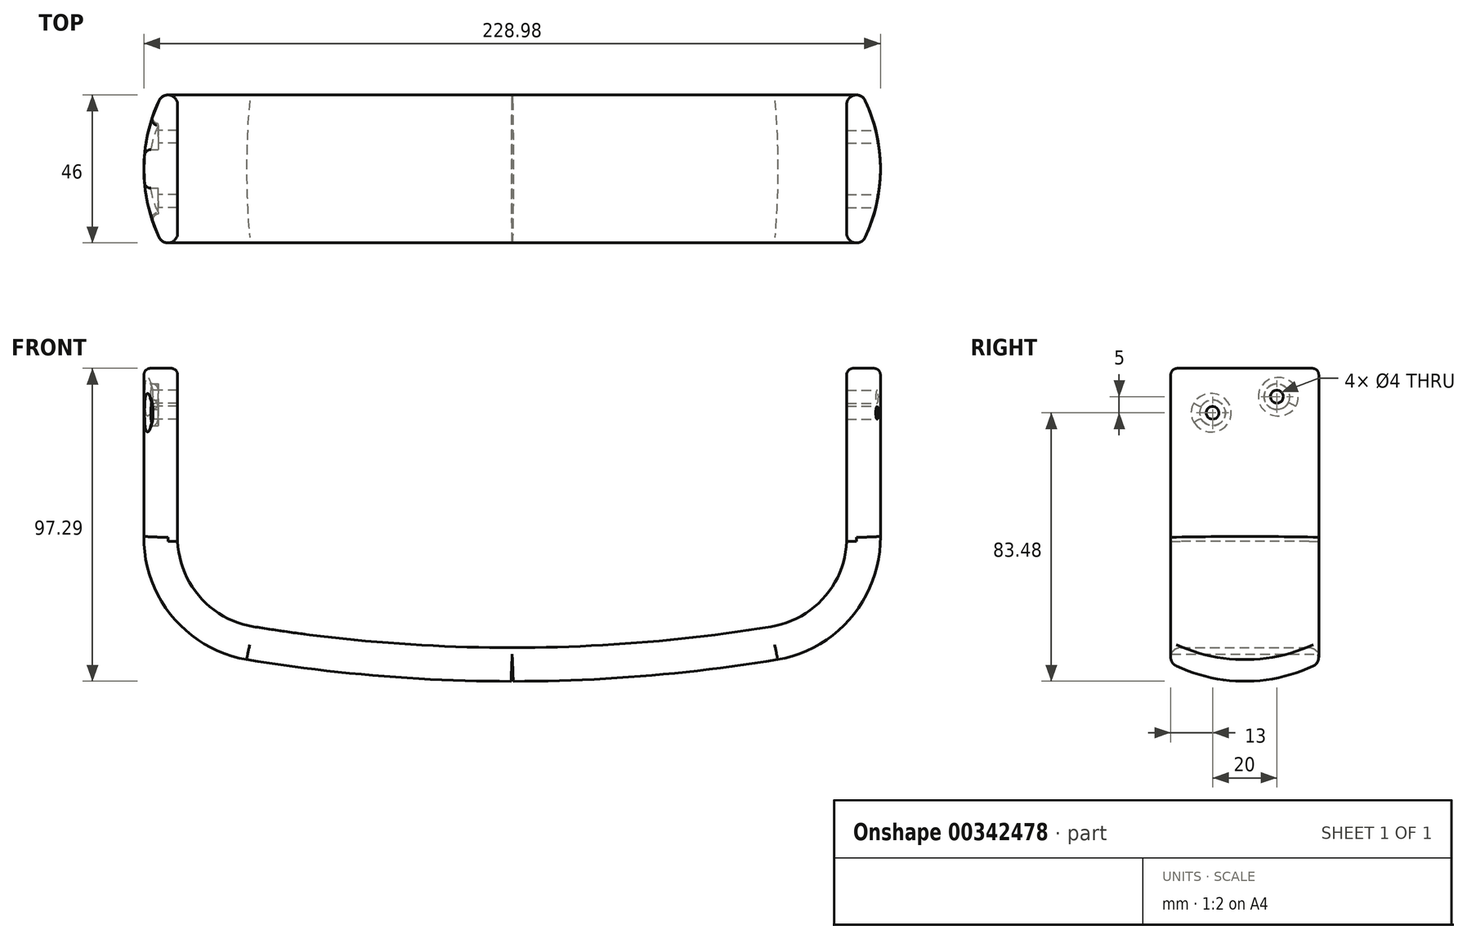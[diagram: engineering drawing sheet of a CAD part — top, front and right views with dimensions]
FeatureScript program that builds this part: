
annotation { "Feature Type Name" : "Feature", "Feature Type Description" : "" }
export const myFeature = defineFeature(function(context is Context, id is Id, definition is map)
    precondition{}
    {
        {
            var Q0;
            Q0=qCreatedBy(makeId("Top.planeOp"),FACE);
            cPlane(context, id + "F0", {"entities" : qUnion([Q0]), "cplaneType" : CPlaneType.OFFSET, "offset" : 55 * mm, "oppositeDirection" : true, "width" : 150 * mm, "height" : 150 * mm});
        }
        {
            var Q0;
            Q0=qCreatedBy(makeId("Front.planeOp"),FACE);
            var sketch = newSketch(context, id + "F1", { "sketchPlane" : qUnion([Q0])});
            skArc(sketch, "E0", {"start": v(0, -90) * mm, "mid": v(-40.56, -88.35) * mm, "end": v(-80.85, -83.42) * mm});
            skLineSegment(sketch, "E1", {"start": v(-106, -53.81) * mm, "end": v(-106, 0) * mm});
            skPoint(sketch, "E2.visualSharp", {"position": v(-106, -78.63) * mm});
            skArc(sketch, "E2.filletArc", {"start": v(-106, -53.81) * mm, "mid": v(-98.86, -73.24) * mm, "end": v(-80.85, -83.42) * mm});
            skArc(sketch, "E3", {"start": v(0, -90) * mm, "mid": v(40.56, -88.35) * mm, "end": v(80.85, -83.42) * mm});
            skLineSegment(sketch, "E4", {"start": v(106, -53.81) * mm, "end": v(106, 0) * mm});
            skPoint(sketch, "E5.visualSharp", {"position": v(106, -78.63) * mm});
            skArc(sketch, "E5.filletArc", {"start": v(80.85, -83.42) * mm, "mid": v(98.86, -73.24) * mm, "end": v(106, -53.81) * mm});
            skSolve(sketch);
        }
        {
            var Q0;
            Q0=qCreatedBy(id+"F0.planeOp",FACE);
            var sketch = newSketch(context, id + "F2", { "sketchPlane" : qUnion([Q0])});
            skCircle(sketch, "E6", {"center": v(-64.47, 0) * mm, "radius": 50 * mm});
            skLineSegment(sketch, "E7", {"start": v(-104, 30.61) * mm, "end": v(-104, -30.61) * mm});
            skCircle(sketch, "E8", {"center": v(-107, 20) * mm, "radius": 3 * mm});
            skCircle(sketch, "E9", {"center": v(-107, -20) * mm, "radius": 3 * mm});
            skSolve(sketch);
        }
        {
            var Q0;
            {var subQ0=sQuery(id+"F2.wireOp",EDGE,"E8");var subQ1=sQuery(id+"F2.wireOp",EDGE,"E6");var subQ2=makeQuery(id+"F2.imprint","INTERSECT",VERTEX,{"derivedFrom":[subQ1,subQ0]});Q0=makeQuery(id+"F2.imprint","IMPRINT",FACE,{"disambiguationData":[TD([[makeQuery(id+"F2.imprint","IMPRINT",EDGE,{"disambiguationData":[TD([[subQ2,-1.0]])],"derivedFrom":subQ1}),1.0]])]});}
            var Q1;
            {var subQ0=sQuery(id+"F2.wireOp",EDGE,"E8");var subQ1=sQuery(id+"F2.wireOp",EDGE,"E7");var subQ2=makeQuery(id+"F2.imprint","INTERSECT",VERTEX,{"disambiguationData":[OD(0.0)],"derivedFrom":[subQ1,subQ0]});Q1=makeQuery(id+"F2.imprint","IMPRINT",FACE,{"disambiguationData":[TD([[makeQuery(id+"F2.imprint","IMPRINT",EDGE,{"disambiguationData":[TD([[subQ2,1.0]])],"derivedFrom":subQ0}),1.0]])]});}
            var Q2;
            {var subQ0=sQuery(id+"F2.wireOp",EDGE,"E9");var subQ1=makeQuery(id+"F2.imprint","INTERSECT",VERTEX,{"derivedFrom":[sQuery(id+"F2.wireOp",EDGE,"E6"),subQ0]});Q2=makeQuery(id+"F2.imprint","IMPRINT",FACE,{"disambiguationData":[TD([[makeQuery(id+"F2.imprint","IMPRINT",EDGE,{"disambiguationData":[TD([[subQ1,1.0]])],"derivedFrom":subQ0}),1.0]])]});}
            var Q3;
            Q3=sQuery(id+"F1.wireOp",EDGE,"E2.filletArc");
            var Q4;
            Q4=sQuery(id+"F1.wireOp",EDGE,"E0");
            sweep(context, id + "F3", {"profiles" : qUnion([Q0, Q1, Q2]), "path" : qUnion([Q3, Q4])});
        }
        {
            var Q0;
            {var subQ0=sQuery(id+"F2.wireOp",EDGE,"E9");var subQ1=makeQuery(id+"F2.imprint","INTERSECT",VERTEX,{"derivedFrom":[sQuery(id+"F2.wireOp",EDGE,"E6"),subQ0]});Q0=makeQuery(id+"F2.imprint","IMPRINT",FACE,{"disambiguationData":[TD([[makeQuery(id+"F2.imprint","IMPRINT",EDGE,{"disambiguationData":[TD([[subQ1,1.0]])],"derivedFrom":subQ0}),1.0]])]});}
            var Q1;
            {var subQ0=sQuery(id+"F2.wireOp",EDGE,"E8");var subQ1=sQuery(id+"F2.wireOp",EDGE,"E6");var subQ2=makeQuery(id+"F2.imprint","INTERSECT",VERTEX,{"derivedFrom":[subQ1,subQ0]});Q1=makeQuery(id+"F2.imprint","IMPRINT",FACE,{"disambiguationData":[TD([[makeQuery(id+"F2.imprint","IMPRINT",EDGE,{"disambiguationData":[TD([[subQ2,-1.0]])],"derivedFrom":subQ1}),1.0]])]});}
            var Q2;
            {var subQ0=sQuery(id+"F2.wireOp",EDGE,"E8");var subQ1=sQuery(id+"F2.wireOp",EDGE,"E7");var subQ2=makeQuery(id+"F2.imprint","INTERSECT",VERTEX,{"disambiguationData":[OD(0.0)],"derivedFrom":[subQ1,subQ0]});Q2=makeQuery(id+"F2.imprint","IMPRINT",FACE,{"disambiguationData":[TD([[makeQuery(id+"F2.imprint","IMPRINT",EDGE,{"disambiguationData":[TD([[subQ2,1.0]])],"derivedFrom":subQ0}),1.0]])]});}
            var Q3;
            Q3=sQuery(id+"F1.wireOp",EDGE,"E1");
            sweep(context, id + "F4", {"operationType" : NewBodyOperationType.ADD, "profiles" : qUnion([Q0, Q1, Q2]), "path" : qUnion([Q3])});
        }
        {
            var Q0;
            Q0=makeQuery(id+"F3.opSweep","SWEPT_BODY",BODY,{"disambiguationData":[OSD([sQuery(id+"F1.wireOp",EDGE,"E0"),sQuery(id+"F2.wireOp",EDGE,"dJ1qTKnS-oq17-yvGb-OPdT-9C4l1Cjw6Oys"),sQuery(id+"F2.wireOp",EDGE,"cmmdOPWz-PyDa-HDoy-eCQN-bhGAXCGdN2CE"),sQuery(id+"F2.wireOp",EDGE,"d8zukWQO-Fq8i-O6NT-Ootf-6UBmwlqmVn10"),sQuery(id+"F2.wireOp",EDGE,"2de68d1f-a85f-48cc-8234-0564c03e4455"),sQuery(id+"F2.wireOp",EDGE,"470c1d83-e3ed-4023-84e1-6bd27dbbabfe"),sQuery(id+"F2.wireOp",EDGE,"wccANr6S-ukYY-3v9n-Jsb8-NzpgIdzZGXg6"),sQuery(id+"F2.wireOp",EDGE,"1fc90554-af48-4865-a39d-4fe91776a1af"),sQuery(id+"F2.wireOp",EDGE,"32e85b6e-5fb4-4d4b-b2f5-fbf4a71d3896")])]});
            var Q1;
            Q1=qCreatedBy(makeId("Right.planeOp"),FACE);
            mirror(context, id + "F5", {"operationType" : NewBodyOperationType.ADD, "entities" : qUnion([Q0]), "mirrorPlane" : qUnion([Q1])});
        }
        {
            var Q0;
            Q0=qCreatedBy(makeId("Right.planeOp"),FACE);
            var sketch = newSketch(context, id + "F6", { "sketchPlane" : qUnion([Q0])});
            skPoint(sketch, "E10", {"position": v(-10, -15) * mm});
            skPoint(sketch, "E11", {"position": v(10, -10) * mm});
            skSolve(sketch);
        }
        {
            var Q0;
            Q0=sQuery(id+"F6.wireOp",VERTEX,"E11");
            var Q1;
            Q1=sQuery(id+"F6.wireOp",VERTEX,"E10");
            var Q2;
            Q2=makeQuery(id+"F3.opSweep","SWEPT_BODY",BODY,{"disambiguationData":[OSD([sQuery(id+"F1.wireOp",EDGE,"E0"),sQuery(id+"F2.wireOp",EDGE,"E6"),sQuery(id+"F2.wireOp",EDGE,"E7"),sQuery(id+"F2.wireOp",EDGE,"E8"),sQuery(id+"F2.wireOp",EDGE,"E9")])]});
            hole(context, id + "F7", {"style" : HoleStyle.SIMPLE, "endStyle" : HoleEndStyle.THROUGH, "holeDiameter" : 4 * mm, "locations" : qUnion([Q0, Q1]), "scope" : qUnion([Q2]), "isTappedThrough" : true});
        }
        {
            var Q0;
            Q0=sQuery(id+"F6.wireOp",VERTEX,"E11");
            var Q1;
            Q1=sQuery(id+"F6.wireOp",VERTEX,"E10");
            var Q2;
            Q2=makeQuery(id+"F3.opSweep","SWEPT_BODY",BODY,{"disambiguationData":[OSD([sQuery(id+"F1.wireOp",EDGE,"E0"),sQuery(id+"F2.wireOp",EDGE,"E6"),sQuery(id+"F2.wireOp",EDGE,"E7"),sQuery(id+"F2.wireOp",EDGE,"E8"),sQuery(id+"F2.wireOp",EDGE,"E9")])]});
            hole(context, id + "F8", {"style" : HoleStyle.SIMPLE, "endStyle" : HoleEndStyle.THROUGH, "oppositeDirection" : true, "holeDiameter" : 4 * mm, "locations" : qUnion([Q0, Q1]), "scope" : qUnion([Q2]), "isTappedThrough" : true});
        }
        {
            var Q0;
            Q0=qCreatedBy(makeId("Right.planeOp"),FACE);
            var sketch = newSketch(context, id + "F9", { "sketchPlane" : qUnion([Q0])});
            skCircle(sketch, "E12", {"center": v(-10, -15) * mm, "radius": 4 * mm});
            skCircle(sketch, "E13", {"center": v(10, -10) * mm, "radius": 4 * mm});
            skSolve(sketch);
        }
        {
            var Q0;
            Q0=qSketchRegion(id+"F9",true);
            extrude(context, id + "F10", {"entities" : qUnion([Q0]), "operationType" : NewBodyOperationType.REMOVE, "oppositeDirection" : true, "depth" : 300 * mm, "hasSecondDirection" : true, "secondDirectionOppositeDirection" : true, "secondDirectionDepth" : 110 * mm});
        }
        {
            var Q0;
            Q0=makeQuery(id+"F4.opSweep","CAP_FACE",FACE,{"disambiguationData":[OSD([sQuery(id+"F1.wireOp",VERTEX,"E1.end"),sQuery(id+"F2.wireOp",EDGE,"dJ1qTKnS-oq17-yvGb-OPdT-9C4l1Cjw6Oys"),sQuery(id+"F2.wireOp",EDGE,"cmmdOPWz-PyDa-HDoy-eCQN-bhGAXCGdN2CE"),sQuery(id+"F2.wireOp",EDGE,"26a42886-8d7c-48d6-a3ba-1dae7db94bb6.filletArc"),sQuery(id+"F2.wireOp",EDGE,"d3881ce3-cca8-404a-a423-4088e6d2d6ec.filletArc")])],"isStart":false});
            var Q1;
            Q1=makeQuery(id+"F5.opPattern","COPY",FACE,{"derivedFrom":makeQuery(id+"F4.opSweep","CAP_FACE",FACE,{"disambiguationData":[OSD([sQuery(id+"F1.wireOp",VERTEX,"E1.end"),sQuery(id+"F2.wireOp",EDGE,"dJ1qTKnS-oq17-yvGb-OPdT-9C4l1Cjw6Oys"),sQuery(id+"F2.wireOp",EDGE,"cmmdOPWz-PyDa-HDoy-eCQN-bhGAXCGdN2CE"),sQuery(id+"F2.wireOp",EDGE,"26a42886-8d7c-48d6-a3ba-1dae7db94bb6.filletArc"),sQuery(id+"F2.wireOp",EDGE,"d3881ce3-cca8-404a-a423-4088e6d2d6ec.filletArc")])],"isStart":false}),"instanceName":"1"});
            var Q2;
            Q2=makeQuery(id+"F10.boolean.opBoolean","INTERSECT",EDGE,{"derivedFrom":[makeQuery(id+"F4.opSweep","SWEPT_FACE",FACE,{"disambiguationData":[OSD([sQuery(id+"F1.wireOp",EDGE,"E1"),sQuery(id+"F2.wireOp",EDGE,"E6")])]}),makeQuery(id+"F10.opExtrude","SWEPT_FACE",FACE,{"disambiguationData":[OSD([sQuery(id+"F9.wireOp",EDGE,"E12")])]})]});
            var Q3;
            Q3=makeQuery(id+"F10.boolean.opBoolean","INTERSECT",EDGE,{"derivedFrom":[makeQuery(id+"F4.opSweep","SWEPT_FACE",FACE,{"disambiguationData":[OSD([sQuery(id+"F1.wireOp",EDGE,"E1"),sQuery(id+"F2.wireOp",EDGE,"E6")])]}),makeQuery(id+"F10.opExtrude","SWEPT_FACE",FACE,{"disambiguationData":[OSD([sQuery(id+"F9.wireOp",EDGE,"E13")])]})]});
            var Q4;
            Q4=makeQuery(id+"FfcVGG5TPQ2WWlo_1.1.F10.boolean.opBoolean","INTERSECT",EDGE,{"derivedFrom":[makeQuery(id+"F5.opPattern","COPY",FACE,{"derivedFrom":makeQuery(id+"F4.opSweep","SWEPT_FACE",FACE,{"disambiguationData":[OSD([sQuery(id+"F1.wireOp",EDGE,"E1"),sQuery(id+"F2.wireOp",EDGE,"E6")])]}),"instanceName":"1"}),makeQuery(id+"FfcVGG5TPQ2WWlo_1.1.F10.opExtrude","SWEPT_FACE",FACE,{"disambiguationData":[OSD([sQuery(id+"F9.wireOp",EDGE,"E12")])]})]});
            var Q5;
            Q5=makeQuery(id+"FfcVGG5TPQ2WWlo_1.1.F10.boolean.opBoolean","INTERSECT",EDGE,{"derivedFrom":[makeQuery(id+"F5.opPattern","COPY",FACE,{"derivedFrom":makeQuery(id+"F4.opSweep","SWEPT_FACE",FACE,{"disambiguationData":[OSD([sQuery(id+"F1.wireOp",EDGE,"E1"),sQuery(id+"F2.wireOp",EDGE,"E6")])]}),"instanceName":"1"}),makeQuery(id+"FfcVGG5TPQ2WWlo_1.1.F10.opExtrude","SWEPT_FACE",FACE,{"disambiguationData":[OSD([sQuery(id+"F9.wireOp",EDGE,"E13")])]})]});
            fillet(context, id + "F11", {"entities" : qUnion([Q0, Q1, Q2, Q3, Q4, Q5]), "radius" : 2 * mm, "tangentPropagation" : true, "allowEdgeOverflow" : false});
        }
    });
